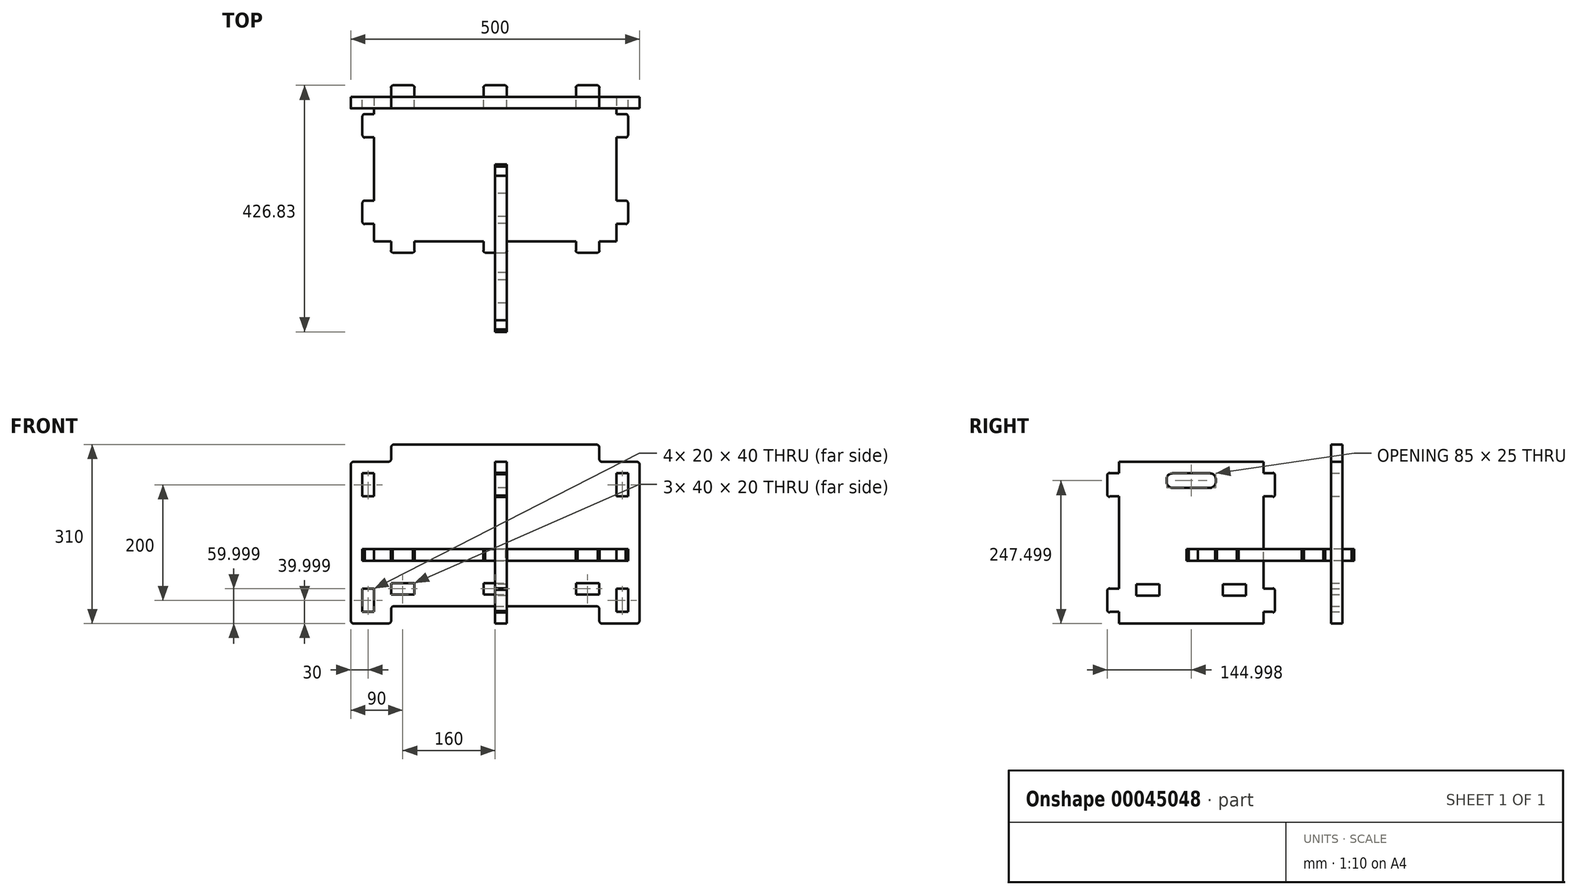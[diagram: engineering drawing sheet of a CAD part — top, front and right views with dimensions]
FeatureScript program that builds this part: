
annotation { "Feature Type Name" : "Feature", "Feature Type Description" : "" }
export const myFeature = defineFeature(function(context is Context, id is Id, definition is map)
    precondition{}
    {
        {
            var Q0;
            Q0=qCreatedBy(makeId("Front.planeOp"),FACE);
            var sketch = newSketch(context, id + "F0", { "sketchPlane" : qUnion([Q0])});
            skLineSegment(sketch, "E0.bottom", {"start": v(-175, -78.55) * mm, "end": v(175, -78.55) * mm});
            skLineSegment(sketch, "E0.top", {"start": v(-245, 171.45) * mm, "end": v(-185, 171.45) * mm});
            skLineSegment(sketch, "E0.left", {"start": v(-250, -80.55) * mm, "end": v(-250, 166.45) * mm});
            skLineSegment(sketch, "E0.right", {"start": v(250, -80.55) * mm, "end": v(250, 166.45) * mm});
            skLineSegment(sketch, "E1.bottom", {"start": v(-250, -78.55) * mm, "end": v(-180, -78.55) * mm});
            skLineSegment(sketch, "E1.top", {"start": v(-245, -108.55) * mm, "end": v(-185, -108.55) * mm});
            skLineSegment(sketch, "E1.left", {"start": v(-250, -78.55) * mm, "end": v(-250, -103.55) * mm});
            skLineSegment(sketch, "E1.right", {"start": v(-180, -83.55) * mm, "end": v(-180, -103.55) * mm});
            skLineSegment(sketch, "E2", {"start": v(0, -78.55) * mm, "end": v(0, 201.45) * mm, "construction": true});
            skLineSegment(sketch, "E3.MirrorCS", {"start": v(250, -78.55) * mm, "end": v(180, -78.55) * mm});
            skLineSegment(sketch, "E4.MirrorCS", {"start": v(245, -108.55) * mm, "end": v(185, -108.55) * mm});
            skLineSegment(sketch, "E5.MirrorCS", {"start": v(250, -78.55) * mm, "end": v(250, -103.55) * mm});
            skLineSegment(sketch, "E6.MirrorCS", {"start": v(180, -83.55) * mm, "end": v(180, -103.55) * mm});
            skLineSegment(sketch, "E7.bottom", {"start": v(-180, 171.45) * mm, "end": v(180, 171.45) * mm});
            skLineSegment(sketch, "E7.top", {"start": v(-175, 201.45) * mm, "end": v(175, 201.45) * mm});
            skLineSegment(sketch, "E7.left", {"start": v(-180, 176.45) * mm, "end": v(-180, 196.45) * mm});
            skLineSegment(sketch, "E7.right", {"start": v(180, 176.45) * mm, "end": v(180, 196.45) * mm});
            skLineSegment(sketch, "E8.bottom", {"start": v(-180, -58.55) * mm, "end": v(-140, -58.55) * mm});
            skLineSegment(sketch, "E8.top", {"start": v(-180, -38.55) * mm, "end": v(-140, -38.55) * mm});
            skLineSegment(sketch, "E8.left", {"start": v(-180, -58.55) * mm, "end": v(-180, -38.55) * mm});
            skLineSegment(sketch, "E8.right", {"start": v(-140, -58.55) * mm, "end": v(-140, -38.55) * mm});
            skLineSegment(sketch, "E9.bottom", {"start": v(-230, -88.55) * mm, "end": v(-210, -88.55) * mm});
            skLineSegment(sketch, "E9.top", {"start": v(-230, -48.55) * mm, "end": v(-210, -48.55) * mm});
            skLineSegment(sketch, "E9.left", {"start": v(-230, -88.55) * mm, "end": v(-230, -48.55) * mm});
            skLineSegment(sketch, "E9.right", {"start": v(-210, -88.55) * mm, "end": v(-210, -48.55) * mm});
            skLineSegment(sketch, "E10.MirrorCS", {"start": v(-210, 151.45) * mm, "end": v(-210, 111.45) * mm});
            skLineSegment(sketch, "E11.MirrorCS", {"start": v(-230, 151.45) * mm, "end": v(-210, 151.45) * mm});
            skLineSegment(sketch, "E12.MirrorCS", {"start": v(-230, 111.45) * mm, "end": v(-210, 111.45) * mm});
            skLineSegment(sketch, "E13.MirrorCS", {"start": v(-230, 151.45) * mm, "end": v(-230, 111.45) * mm});
            skLineSegment(sketch, "E14.MirrorCS", {"start": v(210, -88.55) * mm, "end": v(210, -48.55) * mm});
            skLineSegment(sketch, "E15.MirrorCS", {"start": v(230, -88.55) * mm, "end": v(210, -88.55) * mm});
            skLineSegment(sketch, "E16.MirrorCS", {"start": v(230, -88.55) * mm, "end": v(230, -48.55) * mm});
            skLineSegment(sketch, "E17.MirrorCS", {"start": v(230, -48.55) * mm, "end": v(210, -48.55) * mm});
            skLineSegment(sketch, "E18.MirrorCS", {"start": v(210, 151.45) * mm, "end": v(210, 111.45) * mm});
            skLineSegment(sketch, "E19.MirrorCS", {"start": v(230, 151.45) * mm, "end": v(210, 151.45) * mm});
            skLineSegment(sketch, "E20.MirrorCS", {"start": v(230, 111.45) * mm, "end": v(210, 111.45) * mm});
            skLineSegment(sketch, "E21.MirrorCS", {"start": v(230, 151.45) * mm, "end": v(230, 111.45) * mm});
            skLineSegment(sketch, "E22.MirrorCS", {"start": v(180, -58.55) * mm, "end": v(180, -38.55) * mm});
            skLineSegment(sketch, "E23.MirrorCS", {"start": v(180, -38.55) * mm, "end": v(140, -38.55) * mm});
            skLineSegment(sketch, "E24.MirrorCS", {"start": v(180, -58.55) * mm, "end": v(140, -58.55) * mm});
            skLineSegment(sketch, "E25.MirrorCS", {"start": v(140, -58.55) * mm, "end": v(140, -38.55) * mm});
            skLineSegment(sketch, "E26.bottom", {"start": v(-20, -58.55) * mm, "end": v(20, -58.55) * mm});
            skLineSegment(sketch, "E26.top", {"start": v(-20, -38.55) * mm, "end": v(20, -38.55) * mm});
            skLineSegment(sketch, "E26.left", {"start": v(-20, -58.55) * mm, "end": v(-20, -38.55) * mm});
            skLineSegment(sketch, "E26.right", {"start": v(20, -58.55) * mm, "end": v(20, -38.55) * mm});
            skLineSegment(sketch, "E27", {"start": v(0, -38.55) * mm, "end": v(0, -58.55) * mm, "construction": true});
            skPoint(sketch, "E28.visualSharp", {"position": v(-250, 171.45) * mm});
            skArc(sketch, "E28.filletArc", {"start": v(-245, 171.45) * mm, "mid": v(-248.54, 169.98) * mm, "end": v(-250, 166.45) * mm});
            skPoint(sketch, "E29.visualSharp", {"position": v(250, 171.45) * mm});
            skArc(sketch, "E29.filletArc", {"start": v(250, 166.45) * mm, "mid": v(248.54, 169.98) * mm, "end": v(245, 171.45) * mm});
            skPoint(sketch, "E30.visualSharp", {"position": v(250, -108.55) * mm});
            skArc(sketch, "E30.filletArc", {"start": v(245, -108.55) * mm, "mid": v(248.54, -107.09) * mm, "end": v(250, -103.55) * mm});
            skPoint(sketch, "E31.visualSharp", {"position": v(180, -108.55) * mm});
            skArc(sketch, "E31.filletArc", {"start": v(180, -103.55) * mm, "mid": v(181.46, -107.09) * mm, "end": v(185, -108.55) * mm});
            skPoint(sketch, "E32.visualSharp", {"position": v(-180, -108.55) * mm});
            skArc(sketch, "E32.filletArc", {"start": v(-185, -108.55) * mm, "mid": v(-181.46, -107.09) * mm, "end": v(-180, -103.55) * mm});
            skPoint(sketch, "E33.visualSharp", {"position": v(-250, -108.55) * mm});
            skArc(sketch, "E33.filletArc", {"start": v(-250, -103.55) * mm, "mid": v(-248.54, -107.09) * mm, "end": v(-245, -108.55) * mm});
            skArc(sketch, "E34.filletArc", {"start": v(-185, 171.45) * mm, "mid": v(-181.46, 172.91) * mm, "end": v(-180, 176.45) * mm});
            skPoint(sketch, "E35.visualSharp", {"position": v(-180, 201.45) * mm});
            skArc(sketch, "E35.filletArc", {"start": v(-175, 201.45) * mm, "mid": v(-178.54, 199.98) * mm, "end": v(-180, 196.45) * mm});
            skPoint(sketch, "E36.visualSharp", {"position": v(180, 201.45) * mm});
            skArc(sketch, "E36.filletArc", {"start": v(180, 196.45) * mm, "mid": v(178.54, 199.98) * mm, "end": v(175, 201.45) * mm});
            skLineSegment(sketch, "E37", {"start": v(185, 171.45) * mm, "end": v(245, 171.45) * mm});
            skPoint(sketch, "E38.visualSharp", {"position": v(180, 171.45) * mm});
            skArc(sketch, "E38.filletArc", {"start": v(180, 176.45) * mm, "mid": v(181.46, 172.91) * mm, "end": v(185, 171.45) * mm});
            skPoint(sketch, "E39.newPointA", {"position": v(-180, -80.55) * mm});
            skPoint(sketch, "E39.newPointB", {"position": v(-250, -78.55) * mm});
            skArc(sketch, "E39.filletArc", {"start": v(-175, -78.55) * mm, "mid": v(-178.54, -80.02) * mm, "end": v(-180, -83.55) * mm});
            skPoint(sketch, "E40.newPointA", {"position": v(180, -80.55) * mm});
            skPoint(sketch, "E40.newPointB", {"position": v(250, -78.55) * mm});
            skArc(sketch, "E40.filletArc", {"start": v(180, -83.55) * mm, "mid": v(178.54, -80.02) * mm, "end": v(175, -78.55) * mm});
            skSolve(sketch);
        }
        {
            var Q0;
            Q0=qCreatedBy(makeId("Right.planeOp"),FACE);
            var sketch = newSketch(context, id + "F1", { "sketchPlane" : qUnion([Q0])});
            skLineSegment(sketch, "E41.bottom", {"start": v(0, 196.45) * mm, "end": v(-136.83, 196.45) * mm, "construction": true});
            skLineSegment(sketch, "E41.top", {"start": v(0, -108.55) * mm, "end": v(-136.83, -108.55) * mm, "construction": true});
            skLineSegment(sketch, "E41.left", {"start": v(0, 196.45) * mm, "end": v(0, -108.55) * mm, "construction": true});
            skLineSegment(sketch, "E41.right", {"start": v(-136.83, 196.45) * mm, "end": v(-136.83, -108.55) * mm, "construction": true});
            skLineSegment(sketch, "E42.bottom", {"start": v(-136.83, -108.55) * mm, "end": v(-386.83, -108.55) * mm});
            skLineSegment(sketch, "E42.top", {"start": v(-136.83, 171.45) * mm, "end": v(-386.83, 171.45) * mm});
            skLineSegment(sketch, "E42.left", {"start": v(-136.83, -108.55) * mm, "end": v(-136.83, 171.45) * mm});
            skLineSegment(sketch, "E42.right", {"start": v(-386.83, -108.55) * mm, "end": v(-386.83, 171.45) * mm});
            skLineSegment(sketch, "E43.bottom", {"start": v(-136.83, 151.45) * mm, "end": v(-120.83, 151.45) * mm});
            skLineSegment(sketch, "E43.top", {"start": v(-136.83, 111.45) * mm, "end": v(-120.83, 111.45) * mm});
            skLineSegment(sketch, "E43.left", {"start": v(-136.83, 151.45) * mm, "end": v(-136.83, 111.45) * mm});
            skLineSegment(sketch, "E43.right", {"start": v(-120.83, 151.45) * mm, "end": v(-120.83, 111.45) * mm});
            skLineSegment(sketch, "E44.left", {"start": v(-120.83, 131.45) * mm, "end": v(-120.83, 111.45) * mm});
            skLineSegment(sketch, "E44.right", {"start": v(-116.83, 131.45) * mm, "end": v(-116.83, 112.95) * mm});
            skLineSegment(sketch, "E45", {"start": v(-136.83, 131.45) * mm, "end": v(-116.83, 131.45) * mm, "construction": true});
            skLineSegment(sketch, "E46", {"start": v(-120.83, 111.45) * mm, "end": v(-120.27, 110.9) * mm});
            skLineSegment(sketch, "E47", {"start": v(-118.85, 110.9) * mm, "end": v(-116.83, 112.95) * mm});
            skPoint(sketch, "E48.visualSharp", {"position": v(-119.56, 110.19) * mm});
            skArc(sketch, "E48.filletArc", {"start": v(-120.27, 110.9) * mm, "mid": v(-119.56, 110.6) * mm, "end": v(-118.85, 110.9) * mm});
            skLineSegment(sketch, "E49.MirrorCS", {"start": v(-118.85, 152) * mm, "end": v(-116.83, 149.95) * mm});
            skLineSegment(sketch, "E50.MirrorCS", {"start": v(-120.83, 151.45) * mm, "end": v(-120.27, 152) * mm});
            skArc(sketch, "E51.MirrorCS", {"start": v(-120.27, 152) * mm, "mid": v(-119.56, 152.3) * mm, "end": v(-118.85, 152) * mm});
            skPoint(sketch, "E52.MirrorP", {"position": v(-119.56, 152.7) * mm});
            skLineSegment(sketch, "E53.MirrorCS", {"start": v(-116.83, 131.45) * mm, "end": v(-116.83, 149.95) * mm});
            skLineSegment(sketch, "E54.MirrorCS", {"start": v(-120.83, 131.45) * mm, "end": v(-120.83, 151.45) * mm});
            skLineSegment(sketch, "E55", {"start": v(-386.83, 31.45) * mm, "end": v(-99.55, 31.45) * mm, "construction": true});
            skLineSegment(sketch, "E56.MirrorCS", {"start": v(-120.83, 111.45) * mm, "end": v(-120.83, 151.45) * mm});
            skLineSegment(sketch, "E57.MirrorCS", {"start": v(-136.83, 111.45) * mm, "end": v(-136.83, 151.45) * mm});
            skLineSegment(sketch, "E58.MirrorCS", {"start": v(-386.83, 231.45) * mm, "end": v(-99.55, 231.45) * mm, "construction": true});
            skArc(sketch, "E59.MirrorCS", {"start": v(-120.27, -48) * mm, "mid": v(-119.56, -47.7) * mm, "end": v(-118.85, -48) * mm});
            skLineSegment(sketch, "E60.MirrorCS", {"start": v(-120.83, -48.55) * mm, "end": v(-120.27, -48) * mm});
            skLineSegment(sketch, "E61.MirrorCS", {"start": v(-118.85, -48) * mm, "end": v(-116.83, -50.05) * mm});
            skLineSegment(sketch, "E62.MirrorCS", {"start": v(-118.85, -89.1) * mm, "end": v(-116.83, -87.05) * mm});
            skArc(sketch, "E63.MirrorCS", {"start": v(-120.27, -89.1) * mm, "mid": v(-119.56, -89.4) * mm, "end": v(-118.85, -89.1) * mm});
            skLineSegment(sketch, "E64.MirrorCS", {"start": v(-120.83, -88.55) * mm, "end": v(-120.27, -89.1) * mm});
            skLineSegment(sketch, "E65.MirrorCS", {"start": v(-120.83, -68.55) * mm, "end": v(-120.83, -88.55) * mm});
            skLineSegment(sketch, "E66.MirrorCS", {"start": v(-120.83, -48.55) * mm, "end": v(-120.83, -88.55) * mm});
            skLineSegment(sketch, "E67.MirrorCS", {"start": v(-120.83, -68.55) * mm, "end": v(-120.83, -48.55) * mm});
            skLineSegment(sketch, "E68.MirrorCS", {"start": v(-120.83, -88.55) * mm, "end": v(-120.83, -48.55) * mm});
            skLineSegment(sketch, "E69.MirrorCS", {"start": v(-116.83, -68.55) * mm, "end": v(-116.83, -50.05) * mm});
            skLineSegment(sketch, "E70.MirrorCS", {"start": v(-136.83, -88.55) * mm, "end": v(-120.83, -88.55) * mm});
            skLineSegment(sketch, "E71.MirrorCS", {"start": v(-136.83, -48.55) * mm, "end": v(-120.83, -48.55) * mm});
            skLineSegment(sketch, "E72.MirrorCS", {"start": v(-136.83, -88.55) * mm, "end": v(-136.83, -48.55) * mm});
            skPoint(sketch, "E73.MirrorP", {"position": v(-119.56, -47.3) * mm});
            skLineSegment(sketch, "E74.MirrorCS", {"start": v(-116.83, -68.55) * mm, "end": v(-116.83, -87.05) * mm});
            skLineSegment(sketch, "E75.MirrorCS", {"start": v(-136.83, -48.55) * mm, "end": v(-136.83, -88.55) * mm});
            skPoint(sketch, "E76.MirrorP", {"position": v(-119.56, -89.81) * mm});
            skLineSegment(sketch, "E77.MirrorCS", {"start": v(-136.83, -68.55) * mm, "end": v(-116.83, -68.55) * mm, "construction": true});
            skLineSegment(sketch, "E78", {"start": v(-261.83, 171.45) * mm, "end": v(-261.83, -148.14) * mm, "construction": true});
            skLineSegment(sketch, "E79.MirrorCS", {"start": v(-402.83, -88.55) * mm, "end": v(-403.4, -89.1) * mm});
            skLineSegment(sketch, "E80.MirrorCS", {"start": v(-402.83, -48.55) * mm, "end": v(-403.4, -48) * mm});
            skArc(sketch, "E81.MirrorCS", {"start": v(-403.4, -89.1) * mm, "mid": v(-404.1, -89.4) * mm, "end": v(-404.81, -89.1) * mm});
            skLineSegment(sketch, "E82.MirrorCS", {"start": v(-404.81, -89.1) * mm, "end": v(-406.83, -87.05) * mm});
            skArc(sketch, "E83.MirrorCS", {"start": v(-403.4, -48) * mm, "mid": v(-404.1, -47.7) * mm, "end": v(-404.81, -48) * mm});
            skLineSegment(sketch, "E84.MirrorCS", {"start": v(-404.81, -48) * mm, "end": v(-406.83, -50.05) * mm});
            skLineSegment(sketch, "E85.MirrorCS", {"start": v(-402.83, -48.55) * mm, "end": v(-402.83, -88.55) * mm});
            skLineSegment(sketch, "E86.MirrorCS", {"start": v(-402.83, -68.55) * mm, "end": v(-402.83, -48.55) * mm});
            skLineSegment(sketch, "E87.MirrorCS", {"start": v(-402.83, -68.55) * mm, "end": v(-402.83, -88.55) * mm});
            skLineSegment(sketch, "E88.MirrorCS", {"start": v(-402.83, -88.55) * mm, "end": v(-402.83, -48.55) * mm});
            skPoint(sketch, "E89.MirrorP", {"position": v(-404.1, -47.3) * mm});
            skLineSegment(sketch, "E90.MirrorCS", {"start": v(-386.83, -48.55) * mm, "end": v(-402.83, -48.55) * mm});
            skLineSegment(sketch, "E91.MirrorCS", {"start": v(-406.83, -68.55) * mm, "end": v(-406.83, -87.05) * mm});
            skLineSegment(sketch, "E92.MirrorCS", {"start": v(-386.83, -48.55) * mm, "end": v(-386.83, -88.55) * mm});
            skLineSegment(sketch, "E93.MirrorCS", {"start": v(-386.83, -88.55) * mm, "end": v(-402.83, -88.55) * mm});
            skLineSegment(sketch, "E94.MirrorCS", {"start": v(-406.83, -68.55) * mm, "end": v(-406.83, -50.05) * mm});
            skLineSegment(sketch, "E95.MirrorCS", {"start": v(-386.83, -88.55) * mm, "end": v(-386.83, -48.55) * mm});
            skPoint(sketch, "E96.MirrorP", {"position": v(-404.1, -89.81) * mm});
            skLineSegment(sketch, "E97.MirrorCS", {"start": v(-386.83, -68.55) * mm, "end": v(-406.83, -68.55) * mm, "construction": true});
            skLineSegment(sketch, "E98.MirrorCS", {"start": v(-402.83, 111.45) * mm, "end": v(-403.4, 110.9) * mm});
            skLineSegment(sketch, "E99.MirrorCS", {"start": v(-402.83, 151.45) * mm, "end": v(-403.4, 152) * mm});
            skLineSegment(sketch, "E100.MirrorCS", {"start": v(-404.81, 110.9) * mm, "end": v(-406.83, 112.95) * mm});
            skArc(sketch, "E101.MirrorCS", {"start": v(-403.4, 110.9) * mm, "mid": v(-404.1, 110.6) * mm, "end": v(-404.81, 110.9) * mm});
            skLineSegment(sketch, "E102.MirrorCS", {"start": v(-404.81, 152) * mm, "end": v(-406.83, 149.95) * mm});
            skArc(sketch, "E103.MirrorCS", {"start": v(-403.4, 152) * mm, "mid": v(-404.1, 152.3) * mm, "end": v(-404.81, 152) * mm});
            skLineSegment(sketch, "E104.MirrorCS", {"start": v(-402.83, 111.45) * mm, "end": v(-402.83, 151.45) * mm});
            skLineSegment(sketch, "E105.MirrorCS", {"start": v(-402.83, 131.45) * mm, "end": v(-402.83, 111.45) * mm});
            skLineSegment(sketch, "E106.MirrorCS", {"start": v(-402.83, 131.45) * mm, "end": v(-402.83, 151.45) * mm});
            skLineSegment(sketch, "E107.MirrorCS", {"start": v(-402.83, 151.45) * mm, "end": v(-402.83, 111.45) * mm});
            skPoint(sketch, "E108.MirrorP", {"position": v(-404.1, 110.19) * mm});
            skLineSegment(sketch, "E109.MirrorCS", {"start": v(-386.83, 111.45) * mm, "end": v(-402.83, 111.45) * mm});
            skLineSegment(sketch, "E110.MirrorCS", {"start": v(-386.83, 151.45) * mm, "end": v(-386.83, 111.45) * mm});
            skLineSegment(sketch, "E111.MirrorCS", {"start": v(-406.83, 131.45) * mm, "end": v(-406.83, 112.95) * mm});
            skLineSegment(sketch, "E112.MirrorCS", {"start": v(-386.83, 151.45) * mm, "end": v(-402.83, 151.45) * mm});
            skLineSegment(sketch, "E113.MirrorCS", {"start": v(-406.83, 131.45) * mm, "end": v(-406.83, 149.95) * mm});
            skLineSegment(sketch, "E114.MirrorCS", {"start": v(-386.83, 111.45) * mm, "end": v(-386.83, 151.45) * mm});
            skPoint(sketch, "E115.MirrorP", {"position": v(-404.1, 152.7) * mm});
            skLineSegment(sketch, "E116.MirrorCS", {"start": v(-386.83, 131.45) * mm, "end": v(-406.83, 131.45) * mm, "construction": true});
            skLineSegment(sketch, "E117.bottom", {"start": v(-229.33, 151.45) * mm, "end": v(-294.33, 151.45) * mm});
            skLineSegment(sketch, "E117.top", {"start": v(-229.33, 126.45) * mm, "end": v(-294.33, 126.45) * mm});
            skLineSegment(sketch, "E117.left", {"start": v(-219.33, 141.45) * mm, "end": v(-219.33, 136.45) * mm});
            skLineSegment(sketch, "E117.right", {"start": v(-304.33, 141.45) * mm, "end": v(-304.33, 136.45) * mm});
            skLineSegment(sketch, "E118", {"start": v(-261.83, 151.45) * mm, "end": v(-261.83, 126.45) * mm, "construction": true});
            skPoint(sketch, "E119.visualSharp", {"position": v(-219.33, 151.45) * mm});
            skArc(sketch, "E119.filletArc", {"start": v(-219.33, 141.45) * mm, "mid": v(-222.26, 148.52) * mm, "end": v(-229.33, 151.45) * mm});
            skPoint(sketch, "E120.visualSharp", {"position": v(-219.33, 126.45) * mm});
            skArc(sketch, "E120.filletArc", {"start": v(-229.33, 126.45) * mm, "mid": v(-222.26, 129.38) * mm, "end": v(-219.33, 136.45) * mm});
            skPoint(sketch, "E121.visualSharp", {"position": v(-304.33, 151.45) * mm});
            skArc(sketch, "E121.filletArc", {"start": v(-294.33, 151.45) * mm, "mid": v(-301.4, 148.52) * mm, "end": v(-304.33, 141.45) * mm});
            skPoint(sketch, "E122.visualSharp", {"position": v(-304.33, 126.45) * mm});
            skArc(sketch, "E122.filletArc", {"start": v(-304.33, 136.45) * mm, "mid": v(-301.4, 129.38) * mm, "end": v(-294.33, 126.45) * mm});
            skLineSegment(sketch, "E123.bottom", {"start": v(-356.83, -40.55) * mm, "end": v(-316.83, -40.55) * mm});
            skLineSegment(sketch, "E123.top", {"start": v(-356.83, -60.55) * mm, "end": v(-316.83, -60.55) * mm});
            skLineSegment(sketch, "E123.left", {"start": v(-356.83, -40.55) * mm, "end": v(-356.83, -60.55) * mm});
            skLineSegment(sketch, "E123.right", {"start": v(-316.83, -40.55) * mm, "end": v(-316.83, -60.55) * mm});
            skLineSegment(sketch, "E124.MirrorCS", {"start": v(-166.83, -40.55) * mm, "end": v(-206.83, -40.55) * mm});
            skLineSegment(sketch, "E125.MirrorCS", {"start": v(-166.83, -60.55) * mm, "end": v(-206.83, -60.55) * mm});
            skLineSegment(sketch, "E126.MirrorCS", {"start": v(-166.83, -40.55) * mm, "end": v(-166.83, -60.55) * mm});
            skLineSegment(sketch, "E127.MirrorCS", {"start": v(-206.83, -40.55) * mm, "end": v(-206.83, -60.55) * mm});
            skSolve(sketch);
        }
        {
            var Q0;
            Q0=qCreatedBy(makeId("Top.planeOp"),FACE);
            var sketch = newSketch(context, id + "F2", { "sketchPlane" : qUnion([Q0])});
            skLineSegment(sketch, "E128.bottom", {"start": v(-250, 0) * mm, "end": v(250, 0) * mm, "construction": true});
            skLineSegment(sketch, "E129.bottom", {"start": v(-210, 0) * mm, "end": v(210, 0) * mm});
            skLineSegment(sketch, "E129.top", {"start": v(-210, -250) * mm, "end": v(210, -250) * mm});
            skLineSegment(sketch, "E129.left", {"start": v(-210, 0) * mm, "end": v(-210, -250) * mm});
            skLineSegment(sketch, "E129.right", {"start": v(210, 0) * mm, "end": v(210, -250) * mm});
            skLineSegment(sketch, "E130.bottom", {"start": v(-180, 0) * mm, "end": v(-140, 0) * mm});
            skLineSegment(sketch, "E130.top", {"start": v(-180, 16) * mm, "end": v(-140, 16) * mm});
            skLineSegment(sketch, "E130.left", {"start": v(-180, 0) * mm, "end": v(-180, 16) * mm});
            skLineSegment(sketch, "E130.right", {"start": v(-140, 0) * mm, "end": v(-140, 16) * mm});
            skLineSegment(sketch, "E131.bottom", {"start": v(-180, 16) * mm, "end": v(-160, 16) * mm});
            skLineSegment(sketch, "E131.top", {"start": v(-177.5, 20) * mm, "end": v(-160, 20) * mm});
            skLineSegment(sketch, "E132", {"start": v(-160, 0) * mm, "end": v(-160, 20) * mm, "construction": true});
            skLineSegment(sketch, "E133", {"start": v(-180, 16) * mm, "end": v(-180.26, 16.3) * mm});
            skLineSegment(sketch, "E134", {"start": v(-180.15, 17.7) * mm, "end": v(-177.5, 20) * mm});
            skPoint(sketch, "E135.visualSharp", {"position": v(-180.91, 17.05) * mm});
            skArc(sketch, "E135.filletArc", {"start": v(-180.15, 17.7) * mm, "mid": v(-180.5, 17.02) * mm, "end": v(-180.26, 16.3) * mm});
            skLineSegment(sketch, "E136.MirrorCS", {"start": v(-139.85, 17.7) * mm, "end": v(-142.5, 20) * mm});
            skLineSegment(sketch, "E137.MirrorCS", {"start": v(-140, 16) * mm, "end": v(-139.74, 16.3) * mm});
            skArc(sketch, "E138.MirrorCS", {"start": v(-139.85, 17.7) * mm, "mid": v(-139.5, 17.02) * mm, "end": v(-139.74, 16.3) * mm});
            skLineSegment(sketch, "E139.MirrorCS", {"start": v(-142.5, 20) * mm, "end": v(-160, 20) * mm});
            skLineSegment(sketch, "E140.MirrorCS", {"start": v(-140, 16) * mm, "end": v(-160, 16) * mm});
            skPoint(sketch, "E141.MirrorP", {"position": v(-139.09, 17.05) * mm});
            skLineSegment(sketch, "E142.MirrorCS", {"start": v(180.15, 17.7) * mm, "end": v(177.5, 20) * mm});
            skLineSegment(sketch, "E143.MirrorCS", {"start": v(180, 16) * mm, "end": v(180.26, 16.3) * mm});
            skLineSegment(sketch, "E144.MirrorCS", {"start": v(139.85, 17.7) * mm, "end": v(142.5, 20) * mm});
            skArc(sketch, "E145.MirrorCS", {"start": v(139.85, 17.7) * mm, "mid": v(139.5, 17.02) * mm, "end": v(139.74, 16.3) * mm});
            skArc(sketch, "E146.MirrorCS", {"start": v(180.15, 17.7) * mm, "mid": v(180.5, 17.02) * mm, "end": v(180.26, 16.3) * mm});
            skLineSegment(sketch, "E147.MirrorCS", {"start": v(140, 16) * mm, "end": v(139.74, 16.3) * mm});
            skPoint(sketch, "E148.MirrorP", {"position": v(180.91, 17.05) * mm});
            skLineSegment(sketch, "E149.MirrorCS", {"start": v(180, 16) * mm, "end": v(140, 16) * mm});
            skLineSegment(sketch, "E150.MirrorCS", {"start": v(160, 0) * mm, "end": v(160, 20) * mm, "construction": true});
            skLineSegment(sketch, "E151.MirrorCS", {"start": v(177.5, 20) * mm, "end": v(160, 20) * mm});
            skLineSegment(sketch, "E152.MirrorCS", {"start": v(142.5, 20) * mm, "end": v(160, 20) * mm});
            skLineSegment(sketch, "E153.MirrorCS", {"start": v(180, 16) * mm, "end": v(160, 16) * mm});
            skLineSegment(sketch, "E154.MirrorCS", {"start": v(140, 0) * mm, "end": v(140, 16) * mm});
            skLineSegment(sketch, "E155.MirrorCS", {"start": v(180, 0) * mm, "end": v(180, 16) * mm});
            skLineSegment(sketch, "E156.MirrorCS", {"start": v(180, 0) * mm, "end": v(140, 0) * mm});
            skLineSegment(sketch, "E157.MirrorCS", {"start": v(140, 16) * mm, "end": v(160, 16) * mm});
            skPoint(sketch, "E158.MirrorP", {"position": v(139.09, 17.05) * mm});
            skLineSegment(sketch, "E159", {"start": v(210, -125) * mm, "end": v(-327.24, -125) * mm, "construction": true});
            skPoint(sketch, "E159.endSnap0", {"position": v(-210, -125) * mm});
            skLineSegment(sketch, "E160.MirrorCS", {"start": v(-140, -266) * mm, "end": v(-139.74, -266.3) * mm});
            skLineSegment(sketch, "E161.MirrorCS", {"start": v(-139.85, -267.7) * mm, "end": v(-142.5, -270) * mm});
            skArc(sketch, "E162.MirrorCS", {"start": v(-139.85, -267.7) * mm, "mid": v(-139.5, -267.02) * mm, "end": v(-139.74, -266.3) * mm});
            skLineSegment(sketch, "E163.MirrorCS", {"start": v(-180, -266) * mm, "end": v(-140, -266) * mm});
            skLineSegment(sketch, "E164.MirrorCS", {"start": v(-142.5, -270) * mm, "end": v(-160, -270) * mm});
            skLineSegment(sketch, "E165.MirrorCS", {"start": v(-180, -266) * mm, "end": v(-160, -266) * mm});
            skLineSegment(sketch, "E166.MirrorCS", {"start": v(-140, -266) * mm, "end": v(-160, -266) * mm});
            skLineSegment(sketch, "E167.MirrorCS", {"start": v(-180, -250) * mm, "end": v(-180, -266) * mm});
            skLineSegment(sketch, "E168.MirrorCS", {"start": v(-140, -250) * mm, "end": v(-140, -266) * mm});
            skLineSegment(sketch, "E169.MirrorCS", {"start": v(-180, -250) * mm, "end": v(-140, -250) * mm});
            skLineSegment(sketch, "E170.MirrorCS", {"start": v(-160, -250) * mm, "end": v(-160, -270) * mm, "construction": true});
            skPoint(sketch, "E171.MirrorP", {"position": v(-139.09, -267.05) * mm});
            skLineSegment(sketch, "E172.bottom", {"start": v(-210, -30) * mm, "end": v(-226, -30) * mm});
            skLineSegment(sketch, "E172.top", {"start": v(-210, -70) * mm, "end": v(-226, -70) * mm});
            skLineSegment(sketch, "E172.left", {"start": v(-210, -30) * mm, "end": v(-210, -70) * mm});
            skLineSegment(sketch, "E173", {"start": v(-80, 0) * mm, "end": v(-80, 57.2) * mm, "construction": true});
            skLineSegment(sketch, "E174.MirrorCS", {"start": v(-140, 16) * mm, "end": v(-180, 16) * mm});
            skLineSegment(sketch, "E175.MirrorCS", {"start": v(-140, 0) * mm, "end": v(-180, 0) * mm});
            skLineSegment(sketch, "E176.MirrorCS", {"start": v(20, 16) * mm, "end": v(20.26, 16.3) * mm});
            skArc(sketch, "E177.MirrorCS", {"start": v(20.15, 17.7) * mm, "mid": v(20.5, 17.02) * mm, "end": v(20.26, 16.3) * mm});
            skLineSegment(sketch, "E178.MirrorCS", {"start": v(-20, 16) * mm, "end": v(-20.26, 16.3) * mm});
            skLineSegment(sketch, "E179.MirrorCS", {"start": v(-20.15, 17.7) * mm, "end": v(-17.5, 20) * mm});
            skArc(sketch, "E180.MirrorCS", {"start": v(-20.15, 17.7) * mm, "mid": v(-20.5, 17.02) * mm, "end": v(-20.26, 16.3) * mm});
            skLineSegment(sketch, "E181.MirrorCS", {"start": v(20.15, 17.7) * mm, "end": v(17.5, 20) * mm});
            skLineSegment(sketch, "E182.MirrorCS", {"start": v(-20, 16) * mm, "end": v(0, 16) * mm});
            skLineSegment(sketch, "E183.MirrorCS", {"start": v(20, 16) * mm, "end": v(0, 16) * mm});
            skLineSegment(sketch, "E184.MirrorCS", {"start": v(-20, 0) * mm, "end": v(-20, 16) * mm});
            skLineSegment(sketch, "E185.MirrorCS", {"start": v(20, 0) * mm, "end": v(20, 16) * mm});
            skPoint(sketch, "E186.MirrorP", {"position": v(-20.91, 17.05) * mm});
            skLineSegment(sketch, "E187.MirrorCS", {"start": v(-17.5, 20) * mm, "end": v(0, 20) * mm});
            skLineSegment(sketch, "E188.MirrorCS", {"start": v(20, 0) * mm, "end": v(-20, 0) * mm});
            skLineSegment(sketch, "E189.MirrorCS", {"start": v(17.5, 20) * mm, "end": v(0, 20) * mm});
            skPoint(sketch, "E190.MirrorP", {"position": v(20.91, 17.05) * mm});
            skLineSegment(sketch, "E191.MirrorCS", {"start": v(20, 16) * mm, "end": v(-20, 16) * mm});
            skLineSegment(sketch, "E192.MirrorCS", {"start": v(-20, 0) * mm, "end": v(20, 0) * mm});
            skLineSegment(sketch, "E193.MirrorCS", {"start": v(0, 0) * mm, "end": v(0, 20) * mm, "construction": true});
            skLineSegment(sketch, "E194.MirrorCS", {"start": v(-20, 16) * mm, "end": v(20, 16) * mm});
            skLineSegment(sketch, "E195.MirrorCS", {"start": v(-20, -266) * mm, "end": v(-20.26, -266.3) * mm});
            skLineSegment(sketch, "E196.MirrorCS", {"start": v(20, -266) * mm, "end": v(20.26, -266.3) * mm});
            skArc(sketch, "E197.MirrorCS", {"start": v(-20.15, -267.7) * mm, "mid": v(-20.5, -267.02) * mm, "end": v(-20.26, -266.3) * mm});
            skArc(sketch, "E198.MirrorCS", {"start": v(20.15, -267.7) * mm, "mid": v(20.5, -267.02) * mm, "end": v(20.26, -266.3) * mm});
            skLineSegment(sketch, "E199.MirrorCS", {"start": v(-20.15, -267.7) * mm, "end": v(-17.5, -270) * mm});
            skLineSegment(sketch, "E200.MirrorCS", {"start": v(20.15, -267.7) * mm, "end": v(17.5, -270) * mm});
            skLineSegment(sketch, "E201.MirrorCS", {"start": v(-20, -266) * mm, "end": v(0, -266) * mm});
            skLineSegment(sketch, "E202.MirrorCS", {"start": v(20, -266) * mm, "end": v(0, -266) * mm});
            skLineSegment(sketch, "E203.MirrorCS", {"start": v(17.5, -270) * mm, "end": v(0, -270) * mm});
            skPoint(sketch, "E204.MirrorP", {"position": v(-20.91, -267.05) * mm});
            skLineSegment(sketch, "E205.MirrorCS", {"start": v(-20, -250) * mm, "end": v(20, -250) * mm});
            skPoint(sketch, "E206.MirrorP", {"position": v(20.91, -267.05) * mm});
            skLineSegment(sketch, "E207.MirrorCS", {"start": v(-20, -250) * mm, "end": v(-20, -266) * mm});
            skLineSegment(sketch, "E208.MirrorCS", {"start": v(20, -250) * mm, "end": v(20, -266) * mm});
            skLineSegment(sketch, "E209.MirrorCS", {"start": v(20, -266) * mm, "end": v(-20, -266) * mm});
            skLineSegment(sketch, "E210.MirrorCS", {"start": v(-17.5, -270) * mm, "end": v(0, -270) * mm});
            skLineSegment(sketch, "E211.MirrorCS", {"start": v(-20, -266) * mm, "end": v(20, -266) * mm});
            skLineSegment(sketch, "E212.MirrorCS", {"start": v(20, -250) * mm, "end": v(-20, -250) * mm});
            skLineSegment(sketch, "E213.MirrorCS", {"start": v(0, -250) * mm, "end": v(0, -270) * mm, "construction": true});
            skLineSegment(sketch, "E214", {"start": v(-210, -50) * mm, "end": v(-230, -50) * mm, "construction": true});
            skPoint(sketch, "E215.MirrorP", {"position": v(210, -125) * mm});
            skLineSegment(sketch, "E216", {"start": v(-210, 149.48) * mm, "end": v(210, 149.48) * mm});
            skLineSegment(sketch, "E217", {"start": v(0, 149.48) * mm, "end": v(0, -285.17) * mm, "construction": true});
            skLineSegment(sketch, "E218.MirrorCS", {"start": v(140, -266) * mm, "end": v(139.74, -266.3) * mm});
            skArc(sketch, "E219.MirrorCS", {"start": v(139.85, -267.7) * mm, "mid": v(139.5, -267.02) * mm, "end": v(139.74, -266.3) * mm});
            skLineSegment(sketch, "E220.MirrorCS", {"start": v(139.85, -267.7) * mm, "end": v(142.5, -270) * mm});
            skLineSegment(sketch, "E221.MirrorCS", {"start": v(180, -266) * mm, "end": v(140, -266) * mm});
            skLineSegment(sketch, "E222.MirrorCS", {"start": v(142.5, -270) * mm, "end": v(160, -270) * mm});
            skPoint(sketch, "E223.MirrorP", {"position": v(139.09, -267.05) * mm});
            skLineSegment(sketch, "E224.MirrorCS", {"start": v(140, -250) * mm, "end": v(140, -266) * mm});
            skLineSegment(sketch, "E225.MirrorCS", {"start": v(180, -250) * mm, "end": v(140, -250) * mm});
            skLineSegment(sketch, "E226.MirrorCS", {"start": v(180, -250) * mm, "end": v(180, -266) * mm});
            skLineSegment(sketch, "E227.MirrorCS", {"start": v(160, -250) * mm, "end": v(160, -270) * mm, "construction": true});
            skLineSegment(sketch, "E228.MirrorCS", {"start": v(140, -266) * mm, "end": v(160, -266) * mm});
            skLineSegment(sketch, "E229.MirrorCS", {"start": v(180, -266) * mm, "end": v(160, -266) * mm});
            skLineSegment(sketch, "E230", {"start": v(-226, -70) * mm, "end": v(-226, -30) * mm});
            skLineSegment(sketch, "E231.right", {"start": v(-230, -50) * mm, "end": v(-230, -70) * mm, "construction": true});
            skArc(sketch, "E232.filletArc", {"start": v(-226.23, -29.8) * mm, "mid": v(-226.95, -29.63) * mm, "end": v(-227.59, -30) * mm});
            skLineSegment(sketch, "E233", {"start": v(-226.23, -29.8) * mm, "end": v(-226, -30) * mm});
            skLineSegment(sketch, "E234", {"start": v(-230, -50) * mm, "end": v(-230, -33) * mm});
            skLineSegment(sketch, "E235", {"start": v(-227.59, -30) * mm, "end": v(-230, -33) * mm});
            skLineSegment(sketch, "E236.MirrorCS", {"start": v(-226.23, -70.2) * mm, "end": v(-226, -70) * mm});
            skArc(sketch, "E237.MirrorCS", {"start": v(-226.23, -70.2) * mm, "mid": v(-226.95, -70.37) * mm, "end": v(-227.59, -70) * mm});
            skLineSegment(sketch, "E238.MirrorCS", {"start": v(-227.59, -70) * mm, "end": v(-230, -67) * mm});
            skLineSegment(sketch, "E239.MirrorCS", {"start": v(-230, -50) * mm, "end": v(-230, -67) * mm});
            skLineSegment(sketch, "E240.MirrorCS", {"start": v(-226.23, -220.2) * mm, "end": v(-226, -220) * mm});
            skLineSegment(sketch, "E241.MirrorCS", {"start": v(-226.23, -179.8) * mm, "end": v(-226, -180) * mm});
            skArc(sketch, "E242.MirrorCS", {"start": v(-226.23, -220.2) * mm, "mid": v(-226.95, -220.37) * mm, "end": v(-227.59, -220) * mm});
            skArc(sketch, "E243.MirrorCS", {"start": v(-226.23, -179.8) * mm, "mid": v(-226.95, -179.63) * mm, "end": v(-227.59, -180) * mm});
            skLineSegment(sketch, "E244.MirrorCS", {"start": v(-227.59, -220) * mm, "end": v(-230, -217) * mm});
            skLineSegment(sketch, "E245.MirrorCS", {"start": v(-230, -200) * mm, "end": v(-230, -180) * mm, "construction": true});
            skLineSegment(sketch, "E246.MirrorCS", {"start": v(-227.59, -180) * mm, "end": v(-230, -183) * mm});
            skLineSegment(sketch, "E247.MirrorCS", {"start": v(-226, -180) * mm, "end": v(-226, -220) * mm});
            skLineSegment(sketch, "E248.MirrorCS", {"start": v(-210, -200) * mm, "end": v(-230, -200) * mm, "construction": true});
            skLineSegment(sketch, "E249.MirrorCS", {"start": v(-230, -200) * mm, "end": v(-230, -183) * mm});
            skLineSegment(sketch, "E250.MirrorCS", {"start": v(-210, -220) * mm, "end": v(-226, -220) * mm});
            skLineSegment(sketch, "E251.MirrorCS", {"start": v(-230, -200) * mm, "end": v(-230, -217) * mm});
            skLineSegment(sketch, "E252.MirrorCS", {"start": v(-210, -180) * mm, "end": v(-226, -180) * mm});
            skLineSegment(sketch, "E253.MirrorCS", {"start": v(-210, -220) * mm, "end": v(-210, -180) * mm});
            skLineSegment(sketch, "E254.MirrorCS", {"start": v(-180, -266) * mm, "end": v(-180.26, -266.3) * mm});
            skArc(sketch, "E255.MirrorCS", {"start": v(-180.15, -267.7) * mm, "mid": v(-180.5, -267.02) * mm, "end": v(-180.26, -266.3) * mm});
            skLineSegment(sketch, "E256.MirrorCS", {"start": v(-180.15, -267.7) * mm, "end": v(-177.5, -270) * mm});
            skLineSegment(sketch, "E257.MirrorCS", {"start": v(-177.5, -270) * mm, "end": v(-160, -270) * mm});
            skPoint(sketch, "E258.MirrorP", {"position": v(-180.91, -267.05) * mm});
            skLineSegment(sketch, "E259.MirrorCS", {"start": v(180, -266) * mm, "end": v(180.26, -266.3) * mm});
            skArc(sketch, "E260.MirrorCS", {"start": v(180.15, -267.7) * mm, "mid": v(180.5, -267.02) * mm, "end": v(180.26, -266.3) * mm});
            skLineSegment(sketch, "E261.MirrorCS", {"start": v(180.15, -267.7) * mm, "end": v(177.5, -270) * mm});
            skLineSegment(sketch, "E262.MirrorCS", {"start": v(177.5, -270) * mm, "end": v(160, -270) * mm});
            skPoint(sketch, "E263.MirrorP", {"position": v(180.91, -267.05) * mm});
            skLineSegment(sketch, "E264.MirrorCS", {"start": v(226.23, -29.8) * mm, "end": v(226, -30) * mm});
            skArc(sketch, "E265.MirrorCS", {"start": v(226.23, -29.8) * mm, "mid": v(226.95, -29.63) * mm, "end": v(227.59, -30) * mm});
            skLineSegment(sketch, "E266.MirrorCS", {"start": v(227.59, -70) * mm, "end": v(230, -67) * mm});
            skLineSegment(sketch, "E267.MirrorCS", {"start": v(226.23, -70.2) * mm, "end": v(226, -70) * mm});
            skArc(sketch, "E268.MirrorCS", {"start": v(226.23, -70.2) * mm, "mid": v(226.95, -70.37) * mm, "end": v(227.59, -70) * mm});
            skLineSegment(sketch, "E269.MirrorCS", {"start": v(227.59, -30) * mm, "end": v(230, -33) * mm});
            skLineSegment(sketch, "E270.MirrorCS", {"start": v(230, -50) * mm, "end": v(230, -70) * mm, "construction": true});
            skLineSegment(sketch, "E271.MirrorCS", {"start": v(226, -70) * mm, "end": v(226, -30) * mm});
            skLineSegment(sketch, "E272.MirrorCS", {"start": v(230, -50) * mm, "end": v(230, -67) * mm});
            skLineSegment(sketch, "E273.MirrorCS", {"start": v(210, -30) * mm, "end": v(210, -70) * mm});
            skLineSegment(sketch, "E274.MirrorCS", {"start": v(210, -30) * mm, "end": v(226, -30) * mm});
            skLineSegment(sketch, "E275.MirrorCS", {"start": v(230, -50) * mm, "end": v(230, -33) * mm});
            skLineSegment(sketch, "E276.MirrorCS", {"start": v(210, -50) * mm, "end": v(230, -50) * mm, "construction": true});
            skLineSegment(sketch, "E277.MirrorCS", {"start": v(210, -70) * mm, "end": v(226, -70) * mm});
            skArc(sketch, "E278.MirrorCS", {"start": v(226.23, -220.2) * mm, "mid": v(226.95, -220.37) * mm, "end": v(227.59, -220) * mm});
            skLineSegment(sketch, "E279.MirrorCS", {"start": v(226.23, -179.8) * mm, "end": v(226, -180) * mm});
            skLineSegment(sketch, "E280.MirrorCS", {"start": v(226.23, -220.2) * mm, "end": v(226, -220) * mm});
            skArc(sketch, "E281.MirrorCS", {"start": v(226.23, -179.8) * mm, "mid": v(226.95, -179.63) * mm, "end": v(227.59, -180) * mm});
            skLineSegment(sketch, "E282.MirrorCS", {"start": v(227.59, -180) * mm, "end": v(230, -183) * mm});
            skLineSegment(sketch, "E283.MirrorCS", {"start": v(227.59, -220) * mm, "end": v(230, -217) * mm});
            skLineSegment(sketch, "E284.MirrorCS", {"start": v(230, -200) * mm, "end": v(230, -180) * mm, "construction": true});
            skLineSegment(sketch, "E285.MirrorCS", {"start": v(226, -180) * mm, "end": v(226, -220) * mm});
            skLineSegment(sketch, "E286.MirrorCS", {"start": v(210, -180) * mm, "end": v(226, -180) * mm});
            skLineSegment(sketch, "E287.MirrorCS", {"start": v(230, -200) * mm, "end": v(230, -217) * mm});
            skLineSegment(sketch, "E288.MirrorCS", {"start": v(210, -220) * mm, "end": v(226, -220) * mm});
            skLineSegment(sketch, "E289.MirrorCS", {"start": v(210, -200) * mm, "end": v(230, -200) * mm, "construction": true});
            skLineSegment(sketch, "E290.MirrorCS", {"start": v(210, -220) * mm, "end": v(210, -180) * mm});
            skLineSegment(sketch, "E291.MirrorCS", {"start": v(230, -200) * mm, "end": v(230, -183) * mm});
            skSolve(sketch);
        }
        {
            var Q0;
            Q0 = qSketchRegion(id + "F0", true);
            extrude(context, id + "F3", {"entities" : qUnion([Q0]), "depth" : 20 * mm});
        }
        {
            var Q0;
            Q0 = qSketchRegion(id + "F1", true);
            extrude(context, id + "F4", {"entities" : qUnion([Q0]), "depth" : 20 * mm});
        }
        {
            var Q0;
            Q0 = qSketchRegion(id + "F2", true);
            extrude(context, id + "F5", {"entities" : qUnion([Q0]), "depth" : 20 * mm});
        }
    });
